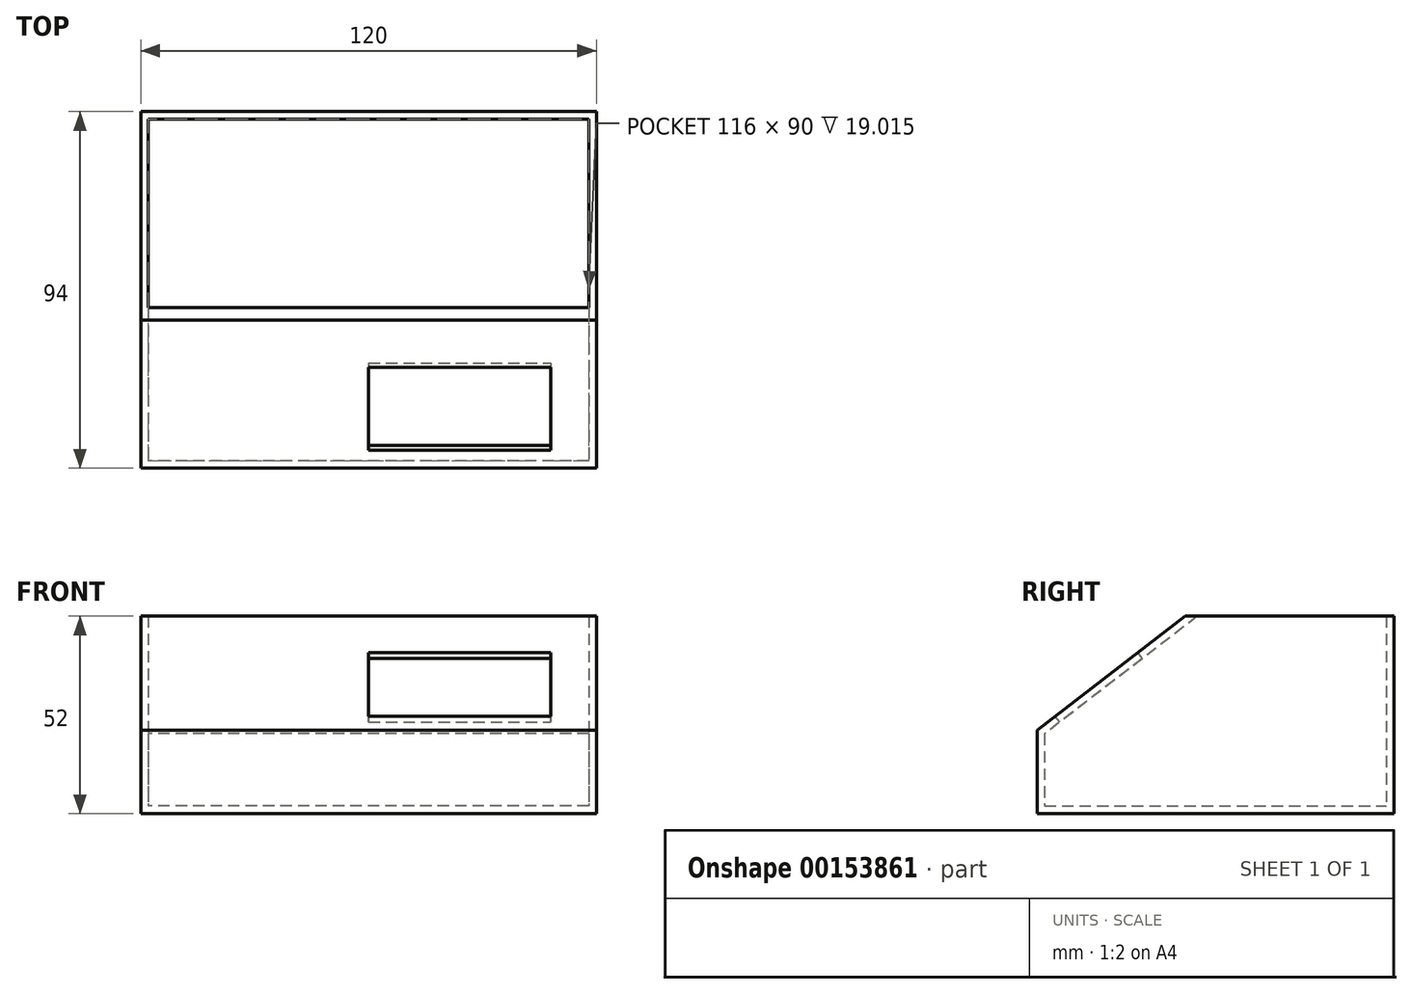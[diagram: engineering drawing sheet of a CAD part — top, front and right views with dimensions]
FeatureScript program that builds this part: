
annotation { "Feature Type Name" : "Feature", "Feature Type Description" : "" }
export const myFeature = defineFeature(function(context is Context, id is Id, definition is map)
    precondition{}
    {
        {
            var Q0;
            Q0=qCreatedBy(makeId("Right.planeOp"),FACE);
            var sketch = newSketch(context, id + "F0", { "sketchPlane" : qUnion([Q0])});
            skLineSegment(sketch, "E0", {"start": v(0, 52) * mm, "end": v(-55, 52) * mm});
            skLineSegment(sketch, "E1", {"start": v(-55, 52) * mm, "end": v(-94, 22) * mm});
            skLineSegment(sketch, "E2", {"start": v(-94, 22) * mm, "end": v(-94, 0) * mm});
            skLineSegment(sketch, "E3", {"start": v(-94, 0) * mm, "end": v(0, 0) * mm});
            skLineSegment(sketch, "E4", {"start": v(0, 52) * mm, "end": v(0, 0) * mm});
            skSolve(sketch);
        }
        {
            var Q0;
            Q0=makeQuery(id+"F0.imprint","IMPRINT",FACE,{"disambiguationData":[TD([[makeQuery(id+"F0.imprint","IMPRINT",EDGE,{"derivedFrom":sQuery(id+"F0.wireOp",EDGE,"E0")}),1.0]])]});
            extrude(context, id + "F1", {"entities" : qUnion([Q0]), "depth" : 120 * mm});
        }
        {
            var Q0;
            Q0=makeQuery(id+"F1.opExtrude","SWEPT_FACE",FACE,{"disambiguationData":[OSD([sQuery(id+"F0.wireOp",EDGE,"E0")])]});
            shell(context, id + "F2", {"entities" : qUnion([Q0]), "thickness" : 2 * mm});
        }
        {
            var Q0;
            Q0=makeQuery(id+"F1.opExtrude","SWEPT_FACE",FACE,{"disambiguationData":[OSD([sQuery(id+"F0.wireOp",EDGE,"E1")])]});
            var sketch = newSketch(context, id + "F3", { "sketchPlane" : qUnion([Q0])});
            skLineSegment(sketch, "E5.bottom", {"start": v(108, -55.1) * mm, "end": v(60, -55.1) * mm});
            skLineSegment(sketch, "E5.top", {"start": v(108, -27.6) * mm, "end": v(60, -27.6) * mm});
            skLineSegment(sketch, "E5.left", {"start": v(108, -55.1) * mm, "end": v(108, -27.6) * mm});
            skLineSegment(sketch, "E5.right", {"start": v(60, -55.1) * mm, "end": v(60, -27.6) * mm});
            skSolve(sketch);
        }
        {
            var Q0;
            Q0=makeQuery(id+"F3.imprint","IMPRINT",FACE,{"disambiguationData":[TD([[makeQuery(id+"F3.imprint","IMPRINT",EDGE,{"derivedFrom":sQuery(id+"F3.wireOp",EDGE,"E5.bottom")}),-1.0]])]});
            extrude(context, id + "F4", {"entities" : qUnion([Q0]), "operationType" : NewBodyOperationType.REMOVE, "oppositeDirection" : true, "depth" : 3 * mm});
        }
    });
